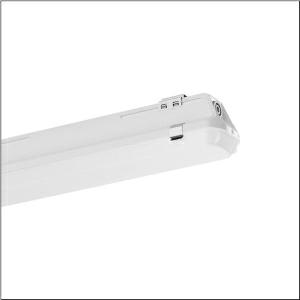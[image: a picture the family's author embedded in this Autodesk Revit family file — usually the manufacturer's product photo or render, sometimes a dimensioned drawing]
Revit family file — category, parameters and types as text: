
# Revit family: monsun_r__11_facade_51ff40mp460h_34d2
name_source: partatom
category: Lighting Fixtures
units: mm (PartAtom-declared; Revit-internal decimal feet)

## family parameters
Cut with Voids When Loaded = No
Host = Face
Light Source = No
Part Type = Normal
Room Calculation Point = No
Round Connector Dimension = Use Diameter
Shared = No

## types (1)
- --- (1 x LED, 6110 lm, 33.5 W, 4000K)
    Apparent Load = 34 VA
    CIE Flux Codes = 47 77 93 95 100
    Color Rendering = 80
    Color Temperature = 4000K
    Default Elevation = 1800 mm
    Description = Monsun® 11 facade, damp-proof luminaire, chain hanger, primary optical cover: enclosure, of PMMA, light emission: direct distribution, primary light characteristic: symmetric, installation type: surface-mounted, horizontal mounting, vertical mounting, LED, rated luminous flux: 6.110lm, luminous efficacy: 182lm/W, light colour: 840, colour temperature: 4000K, control gear: ECG, with terminal, 3-pole, max. 2.5mm², mains connection: 220..240V, AC, 50/60Hz, rated input power: 34W, luminaire housing, of glass-fibre reinforced polyester, uncoated, bright grey, incl. chain hanger, for cables, Ø 8.4..12mm, with climate membrane, length: 1.590mm, width: 90mm, height: 88mm, clip for enclosure, of stainless steel (V2A), ceiling mounting element, of stainless steel (V2A), chain hanger, of stainless steel (V2A), protection rating (complete): IP66, insulation class (complete): insulation class I (protective earthing), certification: CE, ENEC, VDE, UKCA, protection symbol: D, impact resistance: IK06, permissible operating ambient temperature: -35..+50°C, standard: EN 50419, EN 60598-2-1, contact your sales advisor before using the luminaires in applications with unclear chemical exposure, large temperature fluctuations or condensation-forming humidity, LABS conformity tested according to VDMA 24364:2018-05, exposed outdoor area, packaging unit: 1 piece
    Height = 89 mm
    Lamp = 1 x LED
    Lamp Light Flux = 6110 lm
    Lamp Power = 33.5 W
    Lamp count = 1
    Length = 1590 mm
    Luminous efficacy = 182 lm/W
    Manufacturer = Siteco
    ModVariant = No
    Model = 51FF40MP460H
    Mounting Place = Ceiling
    Mounting Type = Surface mounted
    Number of Poles = 1
    OnlyDefault = Yes
    Power Factor = 1
    Product Name = Monsun® 11 facade
    Product group = damp-proof luminaire
    ProductGroupID = 301
    Protection Class = Protection class I
    Protection Degree = IP 66
    RLX_Detail_Level = 1
    RLX_Emergency_Light_Flux = 0 lm
    RLX_Emergency_Type = 0
    RLX_Emergency_Type_DB = No
    RlxData = <blob elided: 89793 chars, md5=5147a120>
    Socket = socket
    Standby Power = 0 W
    System Light Flux = 6110 lm
    System Power = 34 W
    Type Comments = factory setting: luminous flux: 100 % | (A | C | E) | 77 mA
    Type Image = l_1004748.jpg
    URL = http://relux.com
    VarID = @adj_157013
    Voltage = 0 V
    Weight = 0.00 kg
    Width = 90 mm

## geometry (parser evidence)
native form markers: Blend x4, Sweep x13
no freeform markers — native parametric forms only
